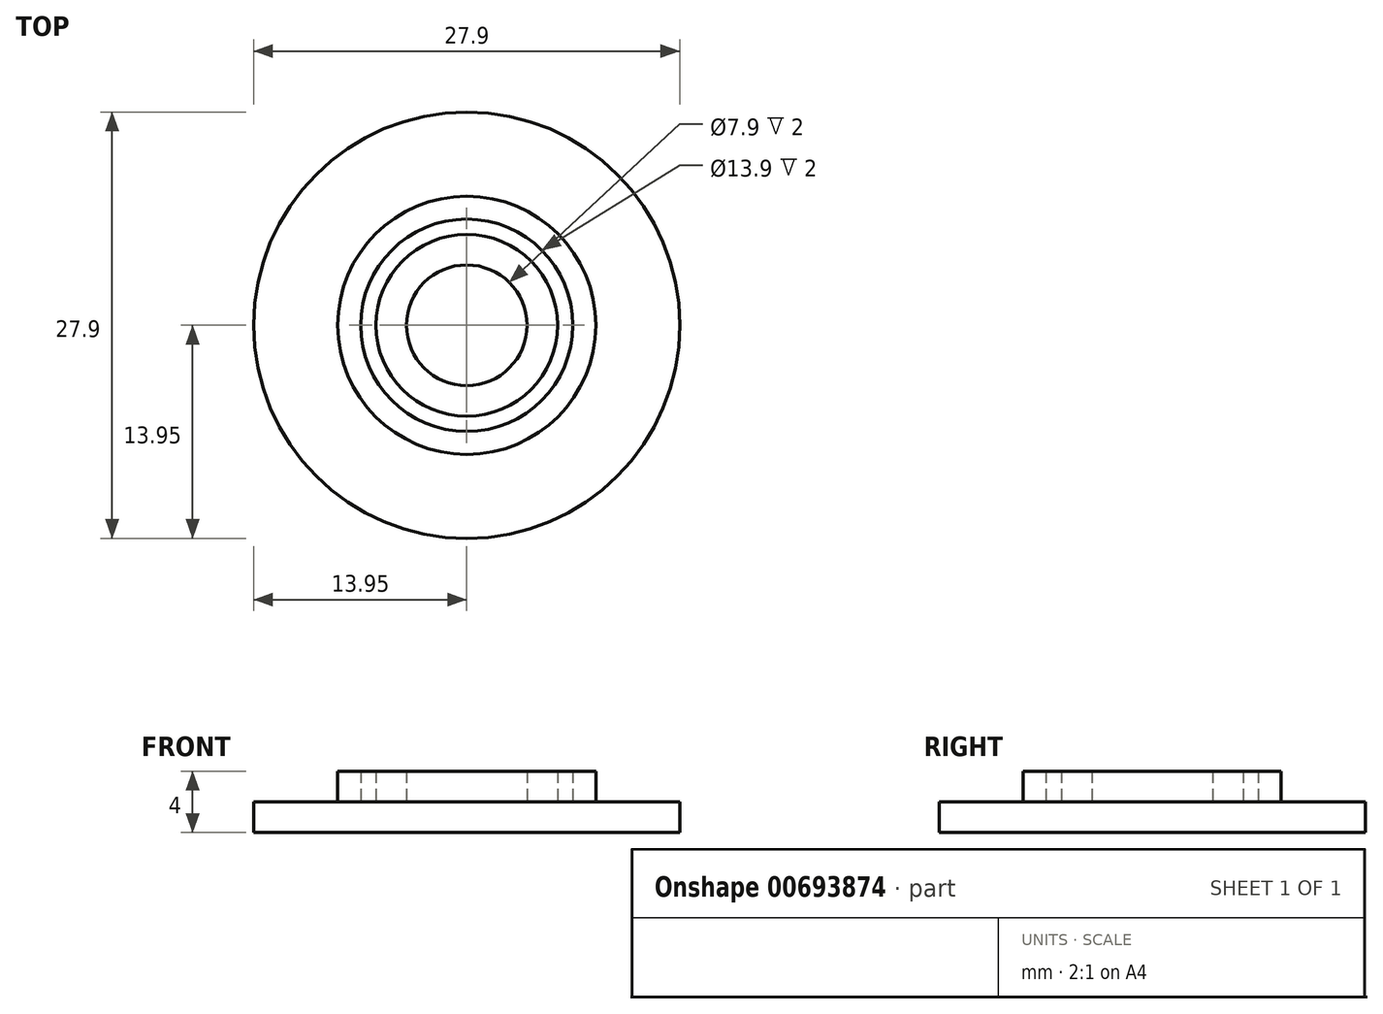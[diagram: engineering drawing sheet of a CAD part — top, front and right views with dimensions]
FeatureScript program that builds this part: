
annotation { "Feature Type Name" : "Feature", "Feature Type Description" : "" }
export const myFeature = defineFeature(function(context is Context, id is Id, definition is map)
    precondition{}
    {
        {
            var Q0;
            Q0=qCreatedBy(makeId("Top.planeOp"),FACE);
            var sketch = newSketch(context, id + "F0", { "sketchPlane" : qUnion([Q0])});
            skCircle(sketch, "E0", {"center": v(0, 0) * mm, "radius": 13.95 * mm});
            skSolve(sketch);
        }
        {
            var Q0;
            Q0 = qSketchRegion(id + "F0", true);
            extrude(context, id + "F1", {"entities" : qUnion([Q0]), "depth" : 2 * mm, "offsetDistance" : 25 * mm});
        }
        {
            var Q0;
            Q0=makeQuery(id+"F1.opExtrude","CAP_FACE",FACE,{"disambiguationData":[OSD([sQuery(id+"F0.wireOp",EDGE,"E0")])],"isStart":false});
            var sketch = newSketch(context, id + "F2", { "sketchPlane" : qUnion([Q0])});
            skCircle(sketch, "E1", {"center": v(0, 0) * mm, "radius": 5.95 * mm});
            skCircle(sketch, "E2", {"center": v(0, 0) * mm, "radius": 3.95 * mm});
            skCircle(sketch, "E3", {"center": v(0, 0) * mm, "radius": 6.95 * mm});
            skCircle(sketch, "E4", {"center": v(0, 0) * mm, "radius": 8.45 * mm});
            skSolve(sketch);
        }
        {
            var Q0;
            Q0=makeQuery(id+"F2.imprint","IMPRINT",FACE,{"disambiguationData":[TD([[makeQuery(id+"F2.imprint","IMPRINT",EDGE,{"derivedFrom":sQuery(id+"F2.wireOp",EDGE,"E1")}),1.0]])]});
            extrude(context, id + "F3", {"entities" : qUnion([Q0]), "operationType" : NewBodyOperationType.ADD, "depth" : 2 * mm, "offsetDistance" : 25 * mm});
        }
        {
            var Q0;
            Q0 = qSketchRegion(id + "F2", true);
            extrude(context, id + "F4", {"entities" : qUnion([Q0]), "operationType" : NewBodyOperationType.ADD, "depth" : 2 * mm, "offsetDistance" : 25 * mm});
        }
    });
